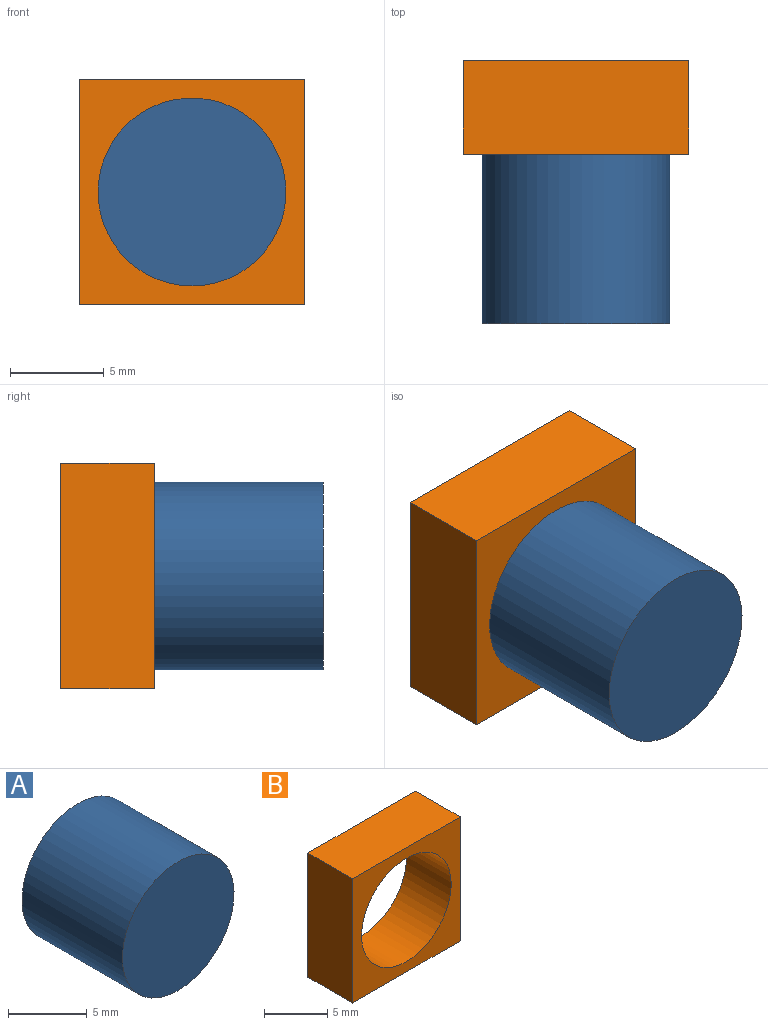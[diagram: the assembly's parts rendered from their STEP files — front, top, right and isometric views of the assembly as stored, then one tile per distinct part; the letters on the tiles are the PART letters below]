
ASSEMBLY  parts=2 mates=1
PART A: 3 faces, bbox 10x9x10 mm
  f0: cylinder r=5mm len=10mm, axis (0,1,0), area 282.7mm2, adj f1,f2
  f1: plane 10x10mm, normal (0,-1,0), area 78.5mm2, adj f0
  f2: plane 10x10mm, normal (0,1,0), area 78.5mm2, adj f0
PART B: 7 faces, bbox 12x5x12 mm
  f0: plane 12x5mm, normal (0,0,-1), area 60mm2, adj f1,f4,f5,f6
  f1: plane 12x5mm, normal (1,0,0), area 60mm2, adj f0,f2,f5,f6
  f2: plane 12x5mm, normal (0,0,1), area 60mm2, adj f1,f4,f5,f6
  f3: cylinder r=5mm len=10mm, axis (0,-1,0), area 157.1mm2, adj f5,f6
  f4: plane 12x5mm, normal (-1,0,0), area 60mm2, adj f0,f2,f5,f6
  f5: plane 12x12mm, normal (0,1,0), area 65.5mm2, adj f0,f1,f2,f3,f4
  f6: plane 12x12mm, normal (0,-1,0), area 65.5mm2, adj f0,f1,f2,f3,f4
PLACE A t=(0.01,-0.39,0.02)mm
PLACE B t=(0.01,-0.39,0.02)mm
MATE fastened A.f0 <-> B.f3  axis (0,1,0) through (0.01,-0.39,0.02)mm
